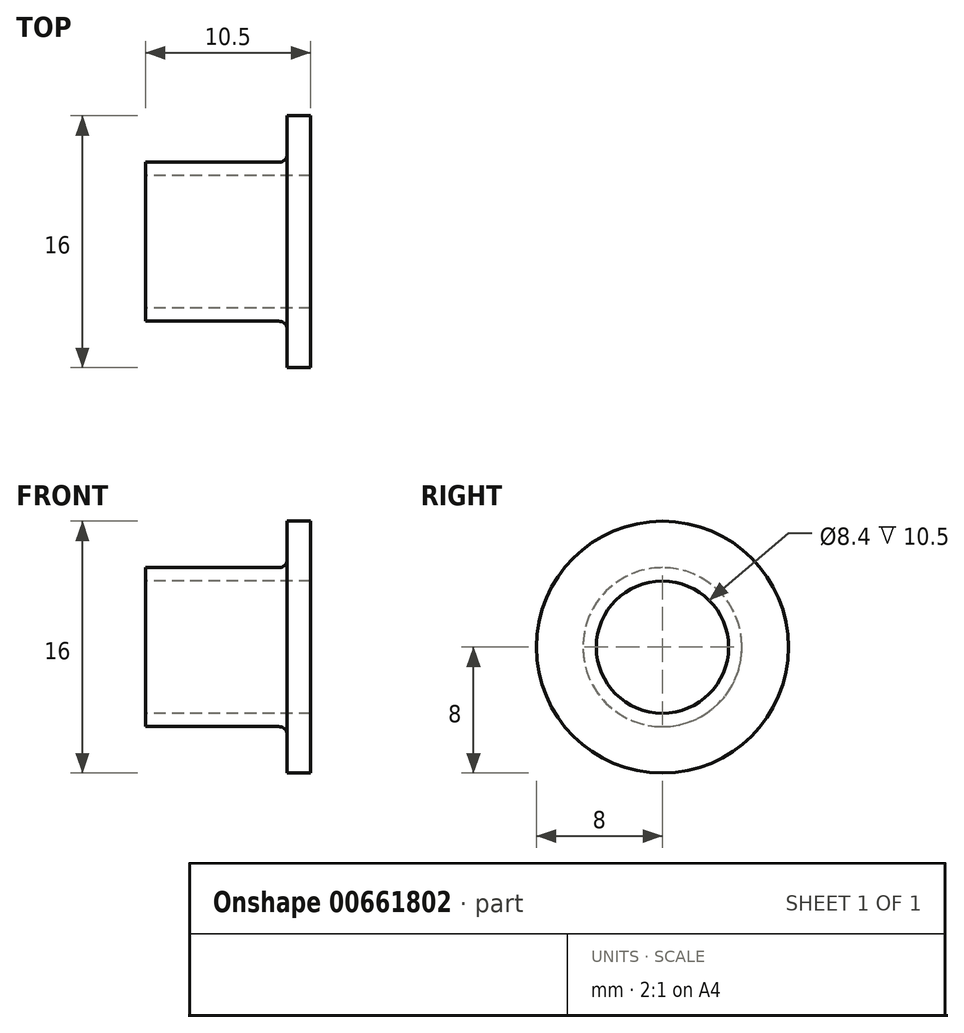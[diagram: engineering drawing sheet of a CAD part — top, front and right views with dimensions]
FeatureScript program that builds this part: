
annotation { "Feature Type Name" : "Feature", "Feature Type Description" : "" }
export const myFeature = defineFeature(function(context is Context, id is Id, definition is map)
    precondition{}
    {
        {
            var Q0;
            Q0=qCreatedBy(makeId("Front.planeOp"),FACE);
            var sketch = newSketch(context, id + "F0", { "sketchPlane" : qUnion([Q0])});
            skLineSegment(sketch, "E0.bottom", {"start": v(-9, 5.05) * mm, "end": v(0, 5.05) * mm});
            skLineSegment(sketch, "E0.left", {"start": v(-9, 5.05) * mm, "end": v(-9, 4.2) * mm});
            skLineSegment(sketch, "E1.bottom", {"start": v(0, 8) * mm, "end": v(1.5, 8) * mm});
            skLineSegment(sketch, "E1.left", {"start": v(0, 8) * mm, "end": v(0, 5.05) * mm});
            skLineSegment(sketch, "E1.right", {"start": v(1.5, 8) * mm, "end": v(1.5, 4.2) * mm});
            skLineSegment(sketch, "E2", {"start": v(-16.64, 0) * mm, "end": v(13.7, 0) * mm, "construction": true});
            skLineSegment(sketch, "E3.MirrorCS", {"start": v(0, -8) * mm, "end": v(1.5, -8) * mm});
            skLineSegment(sketch, "E4.MirrorCS", {"start": v(-9, -5.05) * mm, "end": v(-9, -4.2) * mm});
            skLineSegment(sketch, "E5.MirrorCS", {"start": v(0, -8) * mm, "end": v(0, -5.05) * mm});
            skLineSegment(sketch, "E6.MirrorCS", {"start": v(1.5, -8) * mm, "end": v(1.5, -4.2) * mm});
            skLineSegment(sketch, "E7.MirrorCS", {"start": v(-9, -5.05) * mm, "end": v(0, -5.05) * mm});
            skLineSegment(sketch, "E8", {"start": v(-9, 4.2) * mm, "end": v(1.5, 4.2) * mm});
            skLineSegment(sketch, "E9", {"start": v(-9, -4.2) * mm, "end": v(1.5, -4.2) * mm});
            skSolve(sketch);
        }
        {
            var Q0;
            Q0=makeQuery(id+"F0.imprint","IMPRINT",FACE,{"disambiguationData":[TD([[makeQuery(id+"F0.imprint","IMPRINT",EDGE,{"derivedFrom":sQuery(id+"F0.wireOp",EDGE,"E0.bottom")}),-1.0]])]});
            var Q1;
            Q1=sQuery(id+"F0.wireOp",EDGE,"E2");
            revolve(context, id + "F1", {"entities" : qUnion([Q0]), "axis" : qUnion([Q1]), "revolveType" : RevolveType.FULL});
        }
        {
            var Q0;
            Q0=makeQuery(id+"F1.opRevolve","SWEPT_EDGE",EDGE,{"disambiguationData":[OSD([sQuery(id+"F0.wireOp",EDGE,"E0.bottom"),sQuery(id+"F0.wireOp",EDGE,"E1.left")])]});
            fillet(context, id + "F2", {"entities" : qUnion([Q0]), "radius" : .5 * mm, "tangentPropagation" : true, "allowEdgeOverflow" : false});
        }
    });
